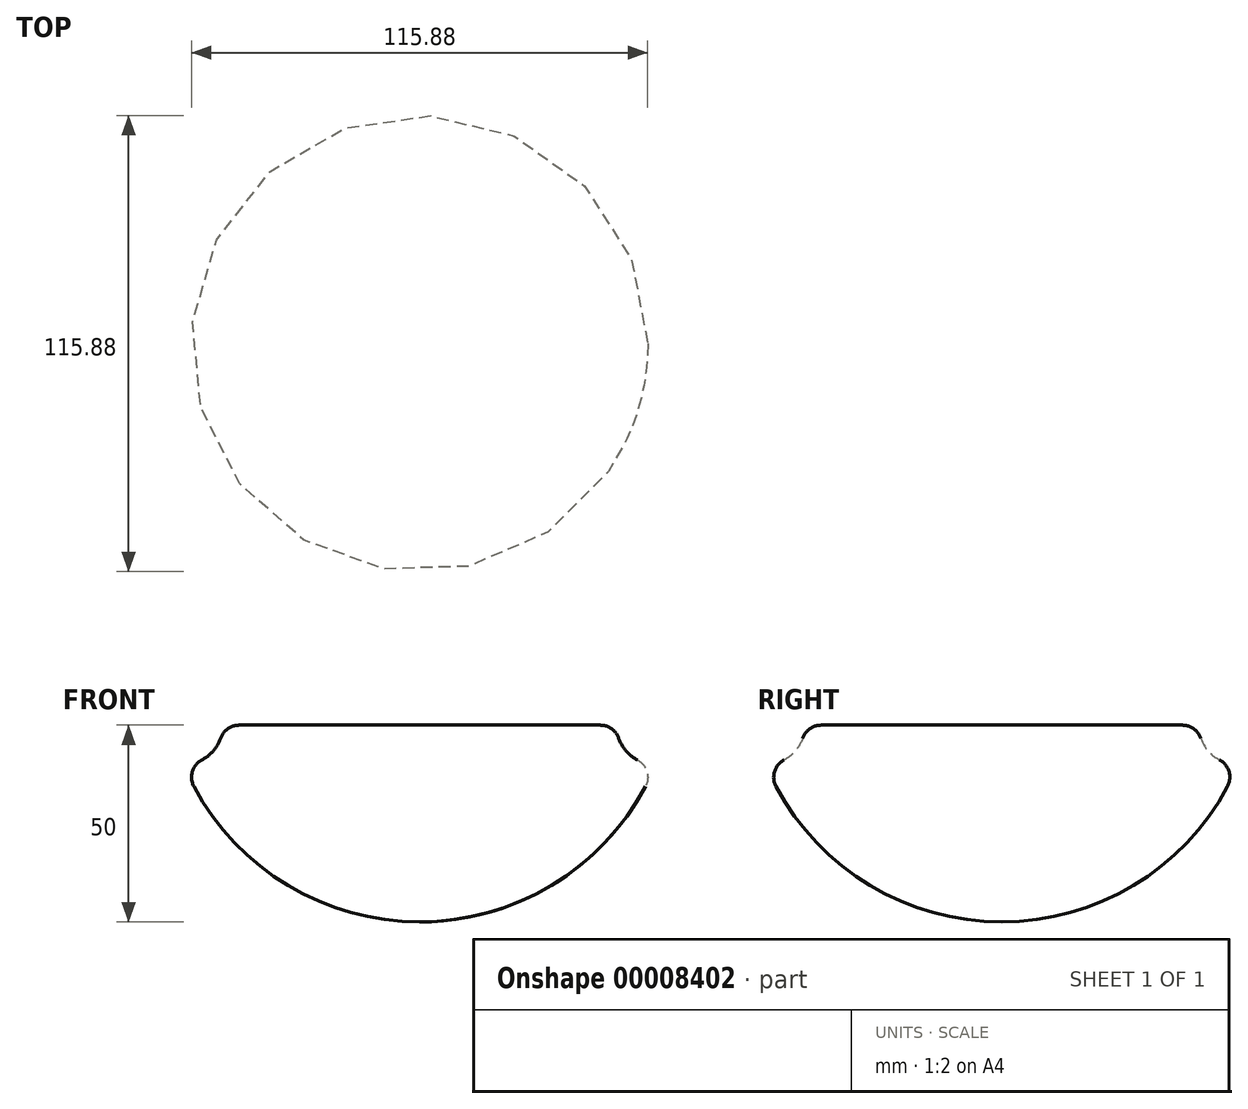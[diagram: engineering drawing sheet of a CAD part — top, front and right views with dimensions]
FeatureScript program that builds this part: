
annotation { "Feature Type Name" : "Feature", "Feature Type Description" : "" }
export const myFeature = defineFeature(function(context is Context, id is Id, definition is map)
    precondition{}
    {
        {
            var Q0;
            Q0=qCreatedBy(makeId("Front.planeOp"),FACE);
            var sketch = newSketch(context, id + "F0", { "sketchPlane" : qUnion([Q0])});
            skArc(sketch, "E0", {"start": v(0, 0) * mm, "mid": v(36.06, 10.92) * mm, "end": v(60, 40) * mm});
            skLineSegment(sketch, "E1", {"start": v(50, 40) * mm, "end": v(60, 40) * mm});
            skLineSegment(sketch, "E2", {"start": v(50, 40) * mm, "end": v(50, 50) * mm});
            skLineSegment(sketch, "E3", {"start": v(50, 50) * mm, "end": v(0, 50) * mm});
            skLineSegment(sketch, "E4", {"start": v(0, 50) * mm, "end": v(0, 0) * mm});
            skSolve(sketch);
        }
        {
            var Q0;
            Q0 = qSketchRegion(id + "F0", true);
            var Q1;
            Q1=sQuery(id+"F0.wireOp",EDGE,"E4");
            revolve(context, id + "F1", {"entities" : qUnion([Q0]), "axis" : qUnion([Q1]), "revolveType" : RevolveType.FULL});
        }
        {
            var Q0;
            Q0=makeQuery(id+"F1.opRevolve","SWEPT_EDGE",EDGE,{"disambiguationData":[OSD([sQuery(id+"F0.wireOp",EDGE,"E1"),sQuery(id+"F0.wireOp",EDGE,"E2")])]});
            fillet(context, id + "F2", {"entities" : qUnion([Q0]), "radius" : 10 * mm, "tangentPropagation" : true, "allowEdgeOverflow" : false});
        }
        {
            var Q0;
            Q0=makeQuery(id+"F2.opFillet","BLEND_EDGE",EDGE,{"blendedFrom":[makeQuery(id+"F1.opRevolve","SWEPT_EDGE",EDGE,{"disambiguationData":[OSD([sQuery(id+"F0.wireOp",EDGE,"E1"),sQuery(id+"F0.wireOp",EDGE,"E2")])]}),makeQuery(id+"F1.opRevolve","SWEPT_FACE",FACE,{"disambiguationData":[OSD([sQuery(id+"F0.wireOp",EDGE,"E0")])]})],"blendedInto":[makeQuery(id+"F1.opRevolve","SWEPT_FACE",FACE,{"disambiguationData":[OSD([sQuery(id+"F0.wireOp",EDGE,"E0")])]})]});
            var Q1;
            Q1=makeQuery(id+"F2.opFillet","BLEND_EDGE",EDGE,{"blendedFrom":[makeQuery(id+"F1.opRevolve","SWEPT_EDGE",EDGE,{"disambiguationData":[OSD([sQuery(id+"F0.wireOp",EDGE,"E1"),sQuery(id+"F0.wireOp",EDGE,"E2")])]}),makeQuery(id+"F1.opRevolve","SWEPT_FACE",FACE,{"disambiguationData":[OSD([sQuery(id+"F0.wireOp",EDGE,"E3")])]})],"blendedInto":[makeQuery(id+"F1.opRevolve","SWEPT_FACE",FACE,{"disambiguationData":[OSD([sQuery(id+"F0.wireOp",EDGE,"E3")])]})]});
            fillet(context, id + "F3", {"entities" : qUnion([Q0, Q1]), "radius" : 5 * mm, "tangentPropagation" : true, "allowEdgeOverflow" : false});
        }
    });
